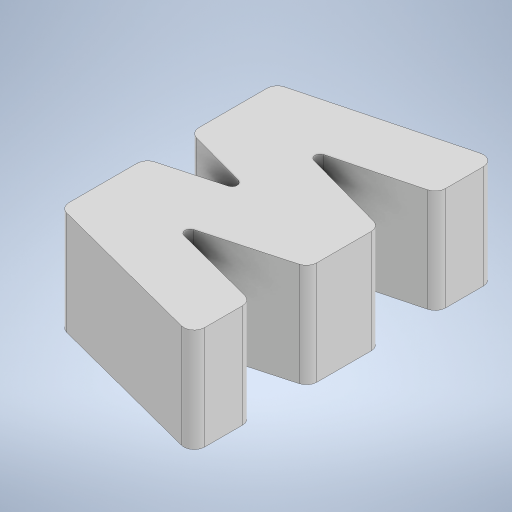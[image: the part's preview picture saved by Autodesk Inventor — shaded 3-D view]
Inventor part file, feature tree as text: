
AUTODESK INVENTOR PART (.ipt)
format: ipt  version: 2023 (Build 270158000, 158)  size: 379,904 bytes
history: native  units: mm
features: extrude x4, sketch x4, projected_geometry x3, other x2
ambient origin geometry x8: Origin, YZ Plane, XZ Plane, XY Plane, X Axis, Y Axis, Z Axis, Center Point
bodies: Body1 (feature_tree), Body2 (feature_tree)
feature tree (13):
  other  "contorno"
  extrude  "Extrusión1"  Depth=0.65mm
  extrude  "Extrusión2"  TaperAngle=30.0deg  [1 undecoded]
  extrude  "Extrusión3"  Depth=7.224mm
  extrude  "Extrusión4"  Depth=22.124mm
  sketch  "Boceto1"  dims[d8=13.0mm d9=0.0mm d17=0.65mm]
  sketch  "Boceto2"  dims[d41=1.3mm d42=30.0deg]
  projected_geometry  "Contorno proyectado1"
  other  "cavidad"
  sketch  "Boceto3"  dims[d43=30.0deg d44=7.224mm]
  projected_geometry  "Contorno proyectado2"
  sketch  "Boceto4"  dims[d47=24.887mm d48=22.124mm d50=8.661mm d51=14.064mm d52=1.2mm d53=13.0mm d54=0.0mm d55=3.4mm d56=0.0mm d57=3.4mm d58=0.0mm]
  projected_geometry  "Contorno proyectado3"
note: 1 required parameter value undecoded (feature->parameter linkage not recoverable at this tier; creation-order binding heuristic only, values carry confidence <= 0.55)
